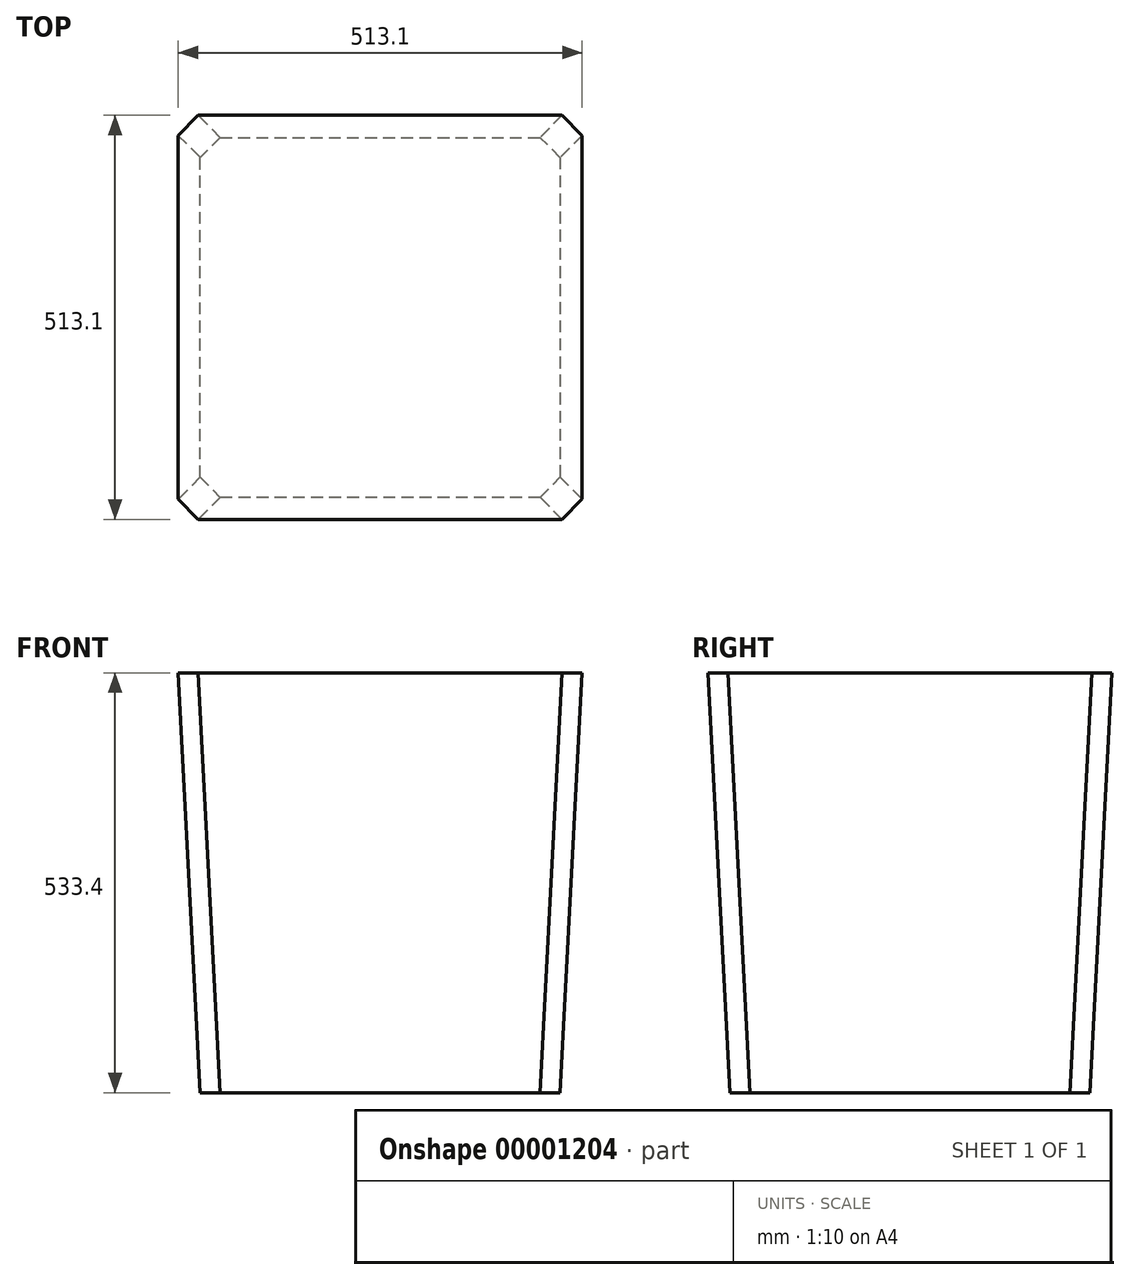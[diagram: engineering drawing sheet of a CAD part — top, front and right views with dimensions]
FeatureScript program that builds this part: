
annotation { "Feature Type Name" : "Feature", "Feature Type Description" : "" }
export const myFeature = defineFeature(function(context is Context, id is Id, definition is map)
    precondition{}
    {
        {
            var Q0;
            Q0=qCreatedBy(makeId("Top.planeOp"),FACE);
            var sketch = newSketch(context, id + "F0", { "sketchPlane" : qUnion([Q0])});
            skLineSegment(sketch, "E0.bottom", {"start": v(0, 0) * mm, "end": v(457.2, 0) * mm});
            skLineSegment(sketch, "E0.top", {"start": v(0, 457.2) * mm, "end": v(457.2, 457.2) * mm});
            skLineSegment(sketch, "E0.left", {"start": v(0, 0) * mm, "end": v(0, 457.2) * mm});
            skLineSegment(sketch, "E0.right", {"start": v(457.2, 0) * mm, "end": v(457.2, 457.2) * mm});
            skSolve(sketch);
        }
        {
            var Q0;
            Q0 = qSketchRegion(id + "F0", true);
            extrude(context, id + "F1", {"entities" : qUnion([Q0]), "depth" : 533.4 * mm, "offsetDistance" : 25.4 * mm, "hasDraft" : true, "draftAngle" : 3 * degree});
        }
        {
            var Q0;
            Q0=makeQuery(id+"F1.opExtrude","SWEPT_EDGE",EDGE,{"disambiguationData":[OSD([sQuery(id+"F0.wireOp",EDGE,"E0.top"),sQuery(id+"F0.wireOp",EDGE,"E0.left")])]});
            var Q1;
            Q1=makeQuery(id+"F1.opExtrude","SWEPT_EDGE",EDGE,{"disambiguationData":[OSD([sQuery(id+"F0.wireOp",EDGE,"E0.bottom"),sQuery(id+"F0.wireOp",EDGE,"E0.left")])]});
            var Q2;
            Q2=makeQuery(id+"F1.opExtrude","SWEPT_EDGE",EDGE,{"disambiguationData":[OSD([sQuery(id+"F0.wireOp",EDGE,"E0.top"),sQuery(id+"F0.wireOp",EDGE,"E0.right")])]});
            var Q3;
            Q3=makeQuery(id+"F1.opExtrude","SWEPT_EDGE",EDGE,{"disambiguationData":[OSD([sQuery(id+"F0.wireOp",EDGE,"E0.bottom"),sQuery(id+"F0.wireOp",EDGE,"E0.right")])]});
            chamfer(context, id + "F2", {"entities" : qUnion([Q0, Q1, Q2, Q3]), "width" : 25.4 * mm, "tangentPropagation" : true});
        }
    });
